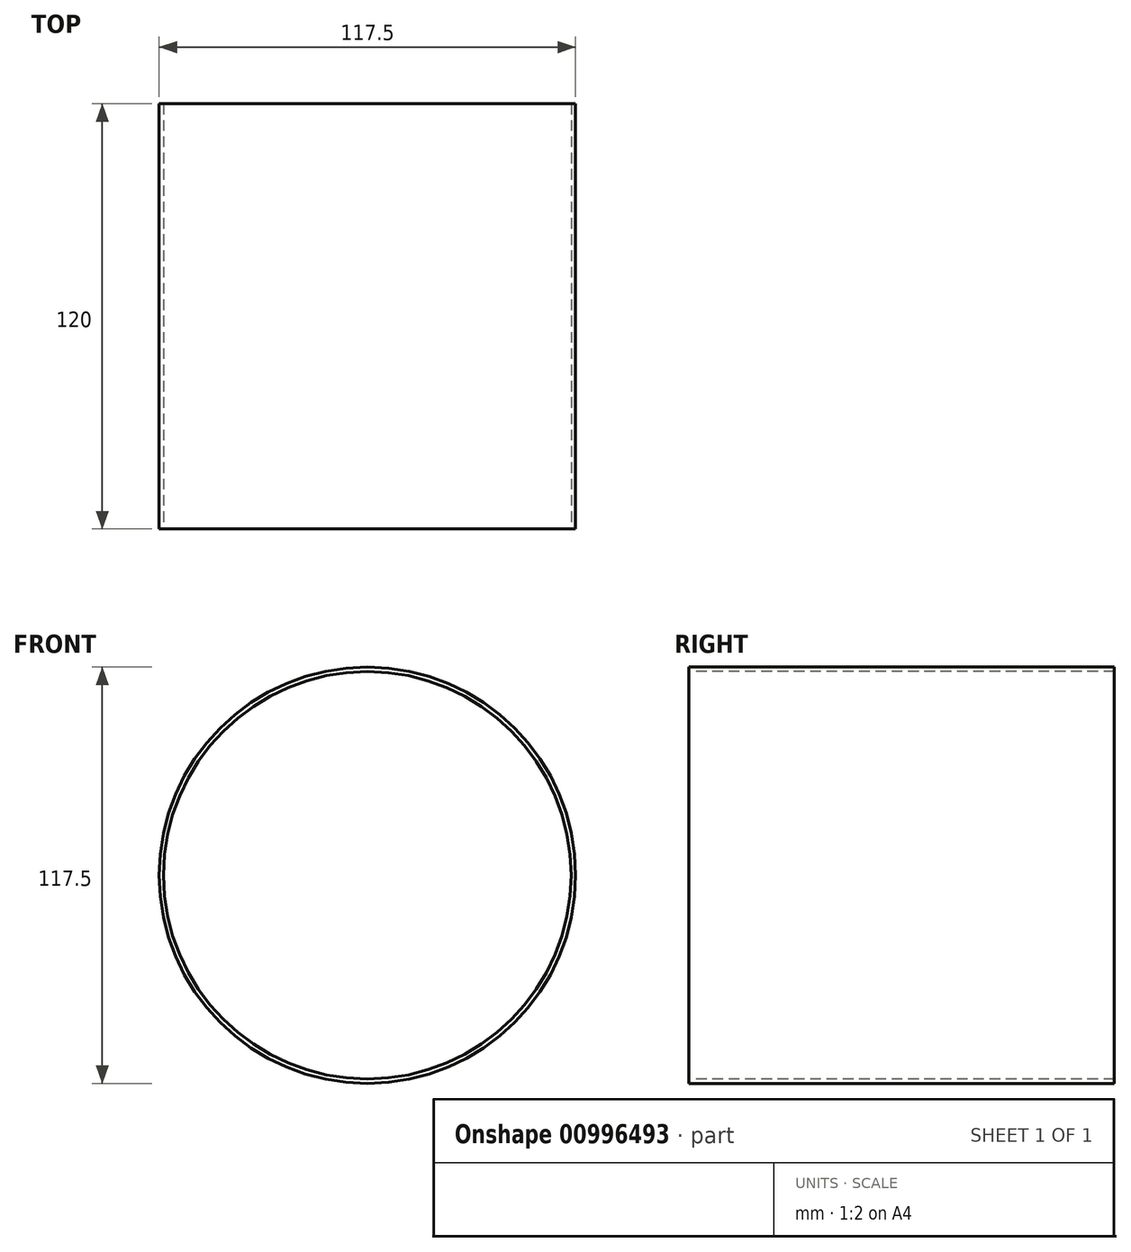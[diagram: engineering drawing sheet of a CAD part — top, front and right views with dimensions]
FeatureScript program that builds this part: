
annotation { "Feature Type Name" : "Feature", "Feature Type Description" : "" }
export const myFeature = defineFeature(function(context is Context, id is Id, definition is map)
    precondition{}
    {
        {
            var Q0;
            Q0=qCreatedBy(makeId("Front.planeOp"),FACE);
            var sketch = newSketch(context, id + "F0", { "sketchPlane" : qUnion([Q0])});
            skCircle(sketch, "E0", {"center": v(0, 0) * mm, "radius": 57.5 * mm});
            skCircle(sketch, "E1", {"center": v(0, 0) * mm, "radius": 58.75 * mm});
            skSolve(sketch);
        }
        {
            var Q0;
            Q0=sQuery(id+"F0.wireOp",EDGE,"E1");
            var Q1;
            Q1=sQuery(id+"F0.wireOp",EDGE,"E0");
            extrude(context, id + "F1", {"bodyType" : ToolBodyType.SURFACE, "surfaceEntities" : qUnion([Q0, Q1]), "depth" : 120 * mm, "offsetDistance" : 25 * mm});
        }
    });
